# Revit family: BuroSeating_Mondo Soho
name_source: partatom
category: Furniture
units: mm (PartAtom-declared; Revit-internal decimal feet)

## family parameters
Always vertical = Yes
Cut with Voids When Loaded = No
OmniClass Number = 23.40.70.14.64.11
OmniClass Title = Office Furniture
Room Calculation Point = No
Shared = Yes
Work Plane-Based = No

## types (2) — shared parameters
Assembly Code = E2020
BackSupportMaterial = BuroSeating_Plastic_Light Grey
CastorWheelMaterial = BuroSeating_Plastic_Dark Grey
FrameMaterial = BuroSeating_Aluminium_Black
Manufacturer = Buro Seating
NominalDepth = 635 mm
NominalHeight = 1210 mm
NominalSeatDepthRange = 450-500d
NominalSeatHeight = 460-560h
NominalWidth = 495 mm
ProductGroup = Soho
ProductPageURL AU = https://buroseating.com
ProductPageURL NZ = https://buroseating.co.nz
ProductRange = Mondo
SeatDepth = 455 mm
SeatLeverFrameMaterial = BuroSeating_Aluminium_Black
SeatLeverHandleMaterial = BuroSeating_Aluminium_Black
SeatTiltMaterial = BuroSeating_Aluminium_Black
SeatWidth = 520 mm
Type Comments = Seat Height 430-520mm High
URL = https://buroseating.co.nz
URL AU = https://buroseating.com
WarrantyDescription = Full 5 year guarantee (excluding upholstery)
zero-valued in all types: Default Elevation

## per-type parameters (varying)
| type | ArmRestMaterial | ArmRestSupportMaterial | BackFrameMaterial | BackPanelMaterial | BackRestMaterial | BaseMaterial | BottomLiftMaterial | CastorMaterial | Description | Model | SeatMaterial | SeatSupportMaterial | TopLiftMaterial |
| Mondo Soho 160A-M3 | BuroSeating_Plastic_Black | BuroSeating_Plastic_Black | BuroSeating_Plastic_Black | BuroSeating_Fabric_Mesh_Black | BuroSeating_Fabric_Mesh_Black | BuroSeating_Aluminium_Black | BuroSeating_Plastic_Black | BuroSeating_Plastic_Black | Mondo Soho Light Grey | 160A-M2 | BuroSeating_Fabric_Black | BuroSeating_Plastic_Black | BuroSeating_Metal_Chrome_Semi-Polished |
| Mondo Soho 160A-M2 | BuroSeating_Plastic_Grey | BuroSeating_Plastic_Light Grey | BuroSeating_Plastic_Light Grey | BuroSeating_Plastic_Light Grey | BuroSeating_Fabric_Mesh_Grey | BuroSeating_Plastic_Light Grey | BuroSeating_Plastic_Light Grey | BuroSeating_Aluminium_Dark Grey | Mondo Soho Black | 160A-M3 | BuroSeating_Fabric_Grey | BuroSeating_Plastic_Light Grey | BuroSeating_Plastic_Light Grey |

## geometry (parser evidence)
native form markers: Sweep x11
no freeform markers — native parametric forms only
